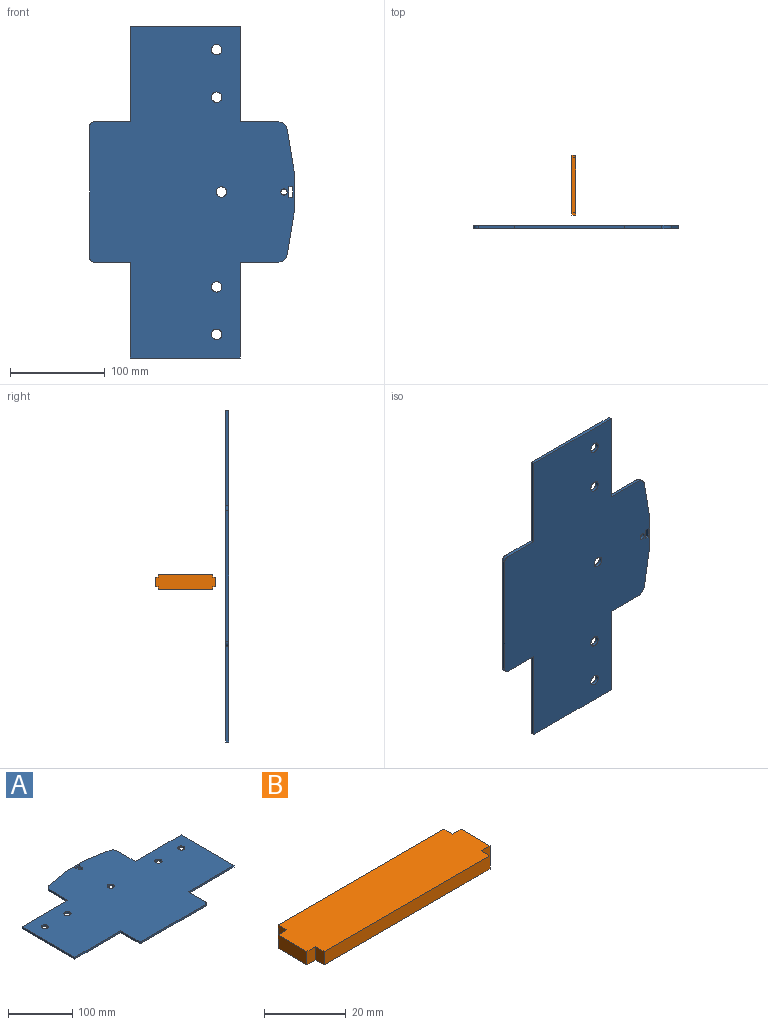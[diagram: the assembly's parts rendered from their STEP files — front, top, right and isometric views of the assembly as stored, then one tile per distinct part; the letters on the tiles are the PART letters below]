
ASSEMBLY  parts=2 mates=1
PART A: 30 faces, bbox 350x216x3.4 mm
  f0: plane 350x216mm, normal (0,0,1), area 54322.1mm2, adj f2,f3,f4,f5,f6,f7,f8,f9
  f1: plane 350x216mm, normal (0,0,-1), area 54322.1mm2, adj f2,f3,f4,f5,f6,f7,f8,f9
  f2: plane 101x3.42mm, normal (0,-1,0), area 345mm2, adj f0,f1,f3,f15
  f3: plane 38x3.42mm, normal (-1,0,0), area 129.8mm2, adj f0,f1,f2,f28
  f4: plane 138x3.42mm, normal (0,-1,0), area 471.4mm2, adj f0,f1,f28,f29
  f5: plane 38x3.42mm, normal (1,0,0), area 129.8mm2, adj f0,f1,f6,f29
  f6: plane 101x3.42mm, normal (0,-1,0), area 345mm2, adj f0,f1,f5,f7
  f7: plane 116x3.42mm, normal (1,0,0), area 396.3mm2, adj f0,f1,f6,f8
  f8: plane 101x3.42mm, normal (0,1,0), area 345mm2, adj f0,f1,f7,f9
  f9: plane 39.53x3.42mm, normal (1,0,0), area 135mm2, adj f0,f1,f8,f26
  f10: plane 45.64x7.61mm, normal (0.16,0.99,0), area 158.1mm2, adj f0,f1,f11,f26
  f11: plane 40x3.42mm, normal (0,1,0), area 136.7mm2, adj f0,f1,f10,f12
  f12: plane 45.64x7.61mm, normal (-0.16,0.99,0), area 158.1mm2, adj f0,f1,f11,f27
  f13: plane 39.53x3.42mm, normal (-1,0,0), area 135mm2, adj f0,f1,f14,f27
  f14: plane 101x3.42mm, normal (0,1,0), area 345mm2, adj f0,f1,f13,f15
  f15: plane 116x3.42mm, normal (-1,0,0), area 396.3mm2, adj f0,f1,f2,f14
  f16: plane 11x3.42mm, normal (0,-1,0), area 37.6mm2, adj f0,f1,f17,f19
  f17: plane 4x3.42mm, normal (1,0,0), area 13.7mm2, adj f0,f1,f16,f18
  f18: plane 11x3.42mm, normal (0,1,0), area 37.6mm2, adj f0,f1,f17,f19
  f19: plane 4x3.42mm, normal (-1,0,0), area 13.7mm2, adj f0,f1,f16,f18
  f20: cylinder r=5.5mm len=11mm, axis (0,0,1), area 118.1mm2, adj f0,f1
  f21: cylinder r=5.5mm len=11mm, axis (0,0,1), area 118.1mm2, adj f0,f1
  f22: cylinder r=5.5mm len=11mm, axis (0,0,1), area 118.1mm2, adj f0,f1
  f23: cylinder r=5.5mm len=11mm, axis (0,0,1), area 118.1mm2, adj f0,f1
  f24: cylinder r=5.5mm len=11mm, axis (0,0,1), area 118.1mm2, adj f0,f1
  f25: cylinder r=3.25mm len=6.5mm, axis (0,0,1), area 69.8mm2, adj f0,f1
  f26: cylinder r=10mm len=9.86mm, axis (0,0,-1), area 48mm2, adj f0,f1,f9,f10
  f27: cylinder r=10mm len=9.86mm, axis (0,0,-1), area 48mm2, adj f0,f1,f12,f13
  f28: cylinder r=5mm len=5mm, axis (0,0,-1), area 26.8mm2, adj f0,f1,f3,f4
  f29: cylinder r=5mm len=5mm, axis (0,0,1), area 26.8mm2, adj f0,f1,f4,f5
PART B: 14 faces, bbox 63.5x16x4 mm
  f0: plane 57.5x3.96mm, normal (0,-1,0), area 227.8mm2, adj f1,f11,f12,f13
  f1: plane 3.96x3mm, normal (1,0,0), area 11.9mm2, adj f0,f2,f12,f13
  f2: plane 3.96x3mm, normal (0,-1,0), area 11.9mm2, adj f1,f3,f12,f13
  f3: plane 10x3.96mm, normal (1,0,0), area 39.6mm2, adj f2,f4,f12,f13
  f4: plane 3.96x3mm, normal (0,1,0), area 11.9mm2, adj f3,f5,f12,f13
  f5: plane 3.96x3mm, normal (1,0,0), area 11.9mm2, adj f4,f6,f12,f13
  f6: plane 57.5x3.96mm, normal (0,1,0), area 227.8mm2, adj f5,f7,f12,f13
  f7: plane 3.96x3mm, normal (-1,0,0), area 11.9mm2, adj f6,f8,f12,f13
  f8: plane 3.96x3mm, normal (0,1,0), area 11.9mm2, adj f7,f9,f12,f13
  f9: plane 10x3.96mm, normal (-1,0,0), area 39.6mm2, adj f8,f10,f12,f13
  f10: plane 3.96x3mm, normal (0,-1,0), area 11.9mm2, adj f9,f11,f12,f13
  f11: plane 3.96x3mm, normal (-1,0,0), area 11.9mm2, adj f0,f10,f12,f13
  f12: plane 63.5x16mm, normal (0,0,1), area 980mm2, adj f0,f1,f2,f3,f4,f5,f6,f7
  f13: plane 63.5x16mm, normal (0,0,-1), area 980mm2, adj f0,f1,f2,f3,f4,f5,f6,f7
PLACE A rot(axis=(0.58,0.58,-0.58),120deg) t=(-112.73,33.11,-16.77)mm
PLACE B rot(axis=(-0.58,-0.58,0.58),120deg) t=(-5.14,75.55,-15.27)mm
MATE slider B.f1 <-> A.f0  axis (0,1,0) through (-9.1,104.3,-16.77)mm
